# Revit family: Domotics-DomesticRanges-GEWISS-CHORUS_COMMAND-THREE-WAY_SWITCH_2M
name_source: partatom
category: Apparecchi elettrici
revit_build: Autodesk Revit 2016 (Build: 20161004_0715(x64)
units: mm (PartAtom-declared; Revit-internal decimal feet)

## family parameters
Condiviso = Sì
Host = Superficie
Mantenere orientamento annotazione = Sì
Numero OmniClass = 23.80.50.11.14
Punto di calcolo locali = No
Quota connettore circolare = Usa diametro
Taglio con vuoti quando caricato = Sì
Tipo di parte = Normale
Titolo OmniClass = Switches

## types (3) — shared parameters
Catalogue = DOMOTICS
Catalogue Range = CHORUS - DOMESTIC RANGE
Distanza_effettiva_x = 1500 mm  [stored 4.92126 ft]
Electrocod = 0131
IDF = 2266ed53-35f0-49de-98f4-7ea16ee829f8
IDT = c454bc21-6205-4e8f-baf1-45f8cd5f8f96
Immagine tipo = GW14123.jpg
Larghezza pulsante = 46 mm  [stored 0.150919 ft]
Produttore = GEWISS S.p.A.
Prospetto di default = 1219 mm
Simbolo_ = SIMBOLO COMMUTATORI : COMM
Technical sheet = https://www.gewiss.com
Tipo_ = CHORUS COMMUTATORI 2M_BASE : GW14123 - Titanio
URL = https://www.gewiss.com
Version file RFA = 19.0
zero-valued in all types: Distanza_x

## per-type parameters (varying)
| type | Descrizione | EAN code | Modello |
| GW12123 - 3-WAY SWITCH, 2M 1P 10AX UP-DOWN BLACK | 3-WAY SWITCH, 2M 1P 10AX UP-DOWN BLACK | 8011564894174 | GW12123 |
| GW10123 - 3-WAY SWITCH, 2M 1P 10AX UP-DOWN WHITE | 3-WAY SWITCH, 2M 1P 10AX UP-DOWN WHITE | 8011564894129 | GW10123 |
| GW14123 - 3-WAY SWITCH 2M 1P 10AX UP-DOWN TITANIUM | 3-WAY SWITCH 2M 1P 10AX UP-DOWN TITANIUM | 8011564894181 | GW14123 |

note: [stored X ft] marks values corroborated as IEEE doubles in the binary element streams (Revit-internal decimal feet)

## geometry (parser evidence)
native form markers: Sweep x1
no freeform markers — native parametric forms only
